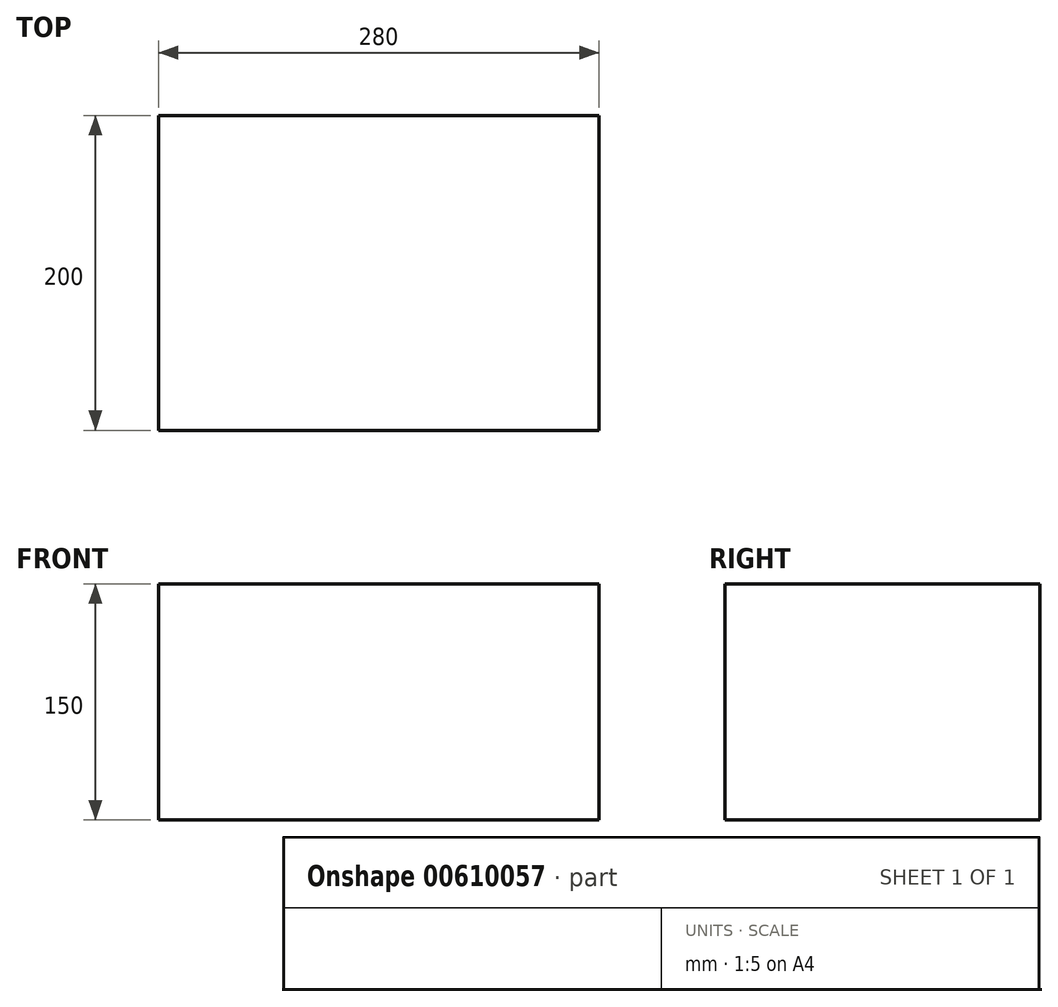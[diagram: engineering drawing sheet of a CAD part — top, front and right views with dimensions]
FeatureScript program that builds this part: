
annotation { "Feature Type Name" : "Feature", "Feature Type Description" : "" }
export const myFeature = defineFeature(function(context is Context, id is Id, definition is map)
    precondition{}
    {
        {
            var Q0;
            Q0=qCreatedBy(makeId("Front.planeOp"),FACE);
            var sketch = newSketch(context, id + "F0", { "sketchPlane" : qUnion([Q0])});
            skLineSegment(sketch, "E0.bottom", {"start": v(0, 0) * mm, "end": v(280, 0) * mm});
            skLineSegment(sketch, "E0.top", {"start": v(0, 150) * mm, "end": v(280, 150) * mm});
            skLineSegment(sketch, "E0.left", {"start": v(0, 0) * mm, "end": v(0, 150) * mm});
            skLineSegment(sketch, "E0.right", {"start": v(280, 0) * mm, "end": v(280, 150) * mm});
            skSolve(sketch);
        }
        {
            var Q0;
            Q0=makeQuery(id+"F0.imprint","IMPRINT",FACE,{"disambiguationData":[TD([[makeQuery(id+"F0.imprint","IMPRINT",EDGE,{"derivedFrom":sQuery(id+"F0.wireOp",EDGE,"E0.bottom")}),1.0]])]});
            extrude(context, id + "F1", {"entities" : qUnion([Q0]), "depth" : 200 * mm, "offsetDistance" : 25 * mm});
        }
    });
